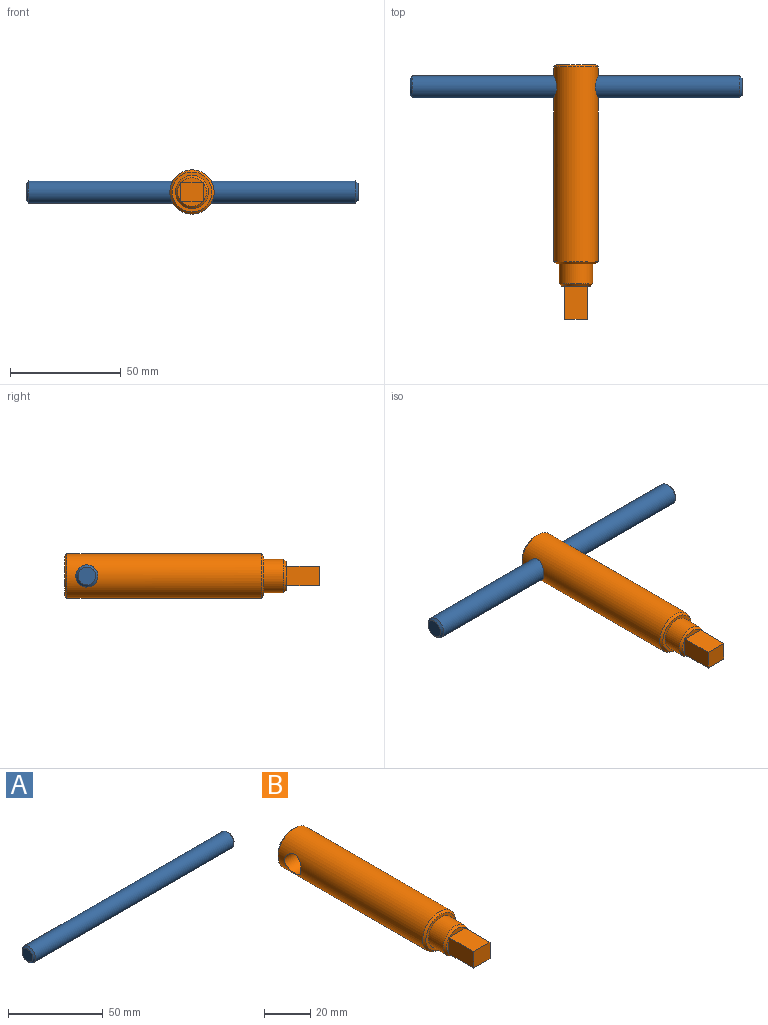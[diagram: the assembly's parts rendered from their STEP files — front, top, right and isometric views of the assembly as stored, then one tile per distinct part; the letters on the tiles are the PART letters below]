
ASSEMBLY  parts=2 mates=1
PART A: 5 faces, bbox 150x10x10 mm
  f0: cylinder r=5mm len=148mm, axis (-1,0,0), area 4649.6mm2, adj f3,f4
  f1: plane 8x8mm, normal (1,0,0), area 50.3mm2, adj f4
  f2: plane 8x8mm, normal (-1,0,0), area 50.3mm2, adj f3
  f3: cone r=5mm half-angle=45deg, axis (1,0,0), area 40mm2, adj f0,f2
  f4: cone r=4mm half-angle=45deg, axis (-1,0,0), area 40mm2, adj f0,f1
PART B: 17 faces, bbox 20x115x20 mm
  f0: plane 9.7x2.17mm, normal (0,-1,0), area 14.6mm2, adj f3,f14
  f1: plane 8.31x1.5mm, normal (0,-1,0), area 8.5mm2, adj f4,f14
  f2: plane 9.7x2.17mm, normal (0,-1,0), area 14.6mm2, adj f5,f14
  f3: plane 15.11x10mm, normal (0,0,-1), area 150mm2, adj f0,f4,f6,f7,f14
  f4: plane 15.11x8.66mm, normal (1,0,0), area 129.9mm2, adj f1,f3,f5,f7,f14
  f5: plane 15.11x10mm, normal (0,0,1), area 150mm2, adj f2,f4,f6,f7,f14
  f6: plane 15.11x8.66mm, normal (-1,0,0), area 129.9mm2, adj f3,f5,f7,f8,f14
  f7: plane 10x8.66mm, normal (0,-1,0), area 86.6mm2, adj f3,f4,f5,f6
  f8: plane 8.31x1.5mm, normal (0,-1,0), area 8.5mm2, adj f6,f14
  f9: cylinder r=7.5mm len=15mm, axis (0,-1,0), area 424.1mm2, adj f12,f14
  f10: cylinder r=10mm len=88mm, axis (0,-1,0), area 5366.5mm2, adj f13,f15,f16
  f11: plane 18x18mm, normal (0,1,0), area 254.5mm2, adj f16
  f12: plane 18x18mm, normal (0,-1,0), area 77.8mm2, adj f9,f15
  f13: cylinder r=5mm len=20mm, axis (1,0,0), area 587mm2, adj f10
  f14: cone r=7.5mm half-angle=45deg, axis (0,1,0), area 62.1mm2, adj f0,f1,f2,f3,f4,f5,f6,f8
  f15: cone r=9mm half-angle=45deg, axis (0,1,0), area 84.4mm2, adj f10,f12
  f16: cone r=10mm half-angle=45deg, axis (0,-1,0), area 84.4mm2, adj f10,f11
PLACE A t=(66.41,75.37,40.53)mm
PLACE B t=(66.41,-14.63,40.53)mm
MATE planar A.f0 <-> B.f13  axis (-1,0,0) through (66.41,75.37,40.53)mm
